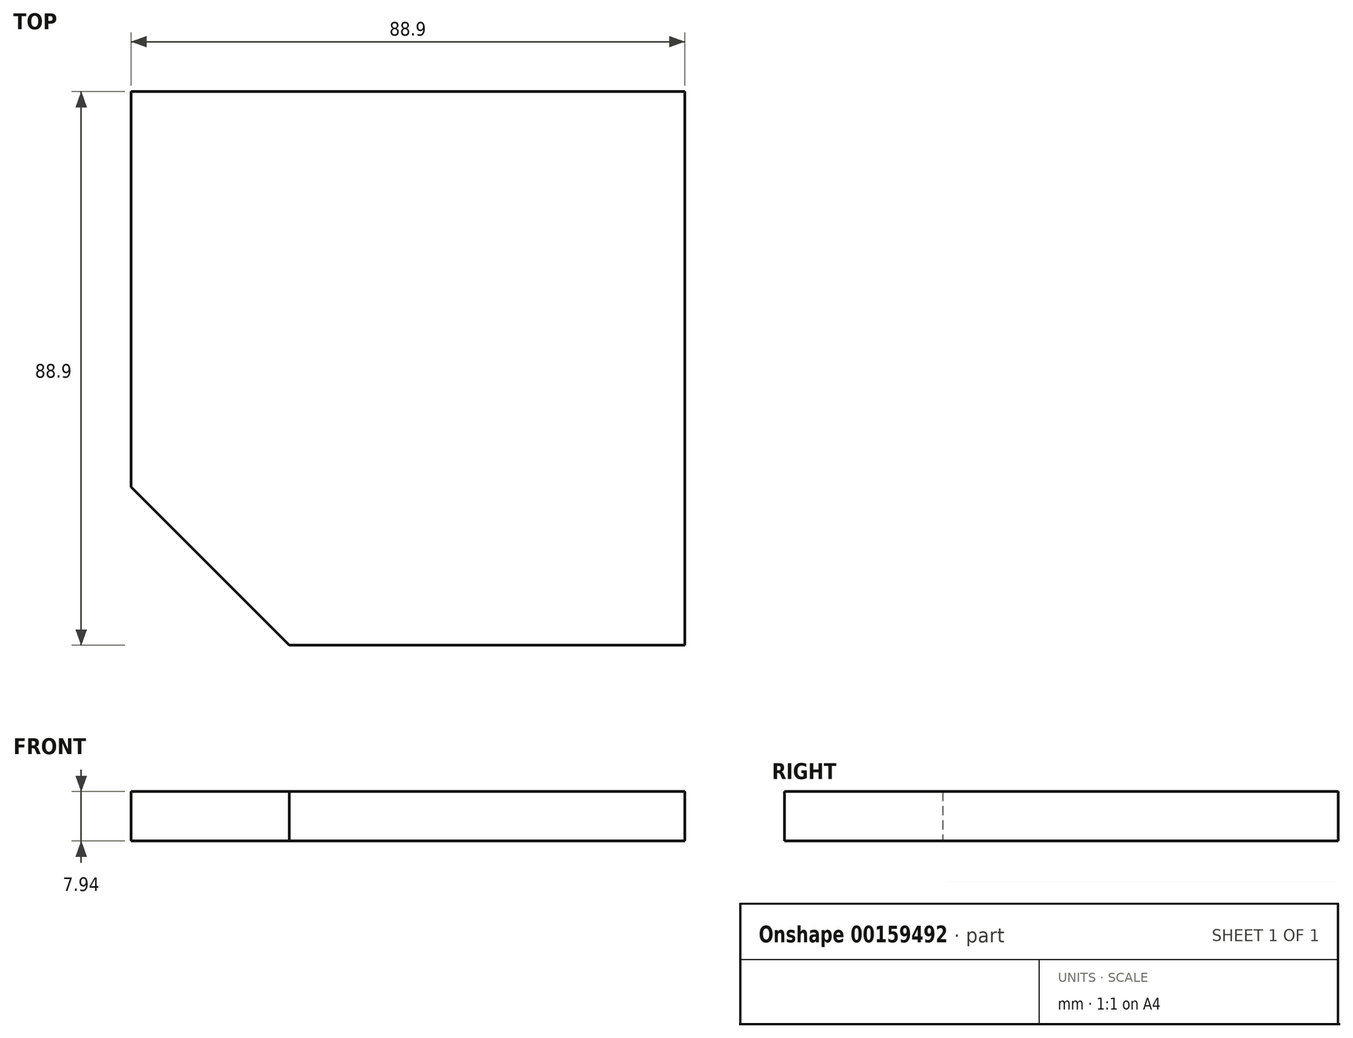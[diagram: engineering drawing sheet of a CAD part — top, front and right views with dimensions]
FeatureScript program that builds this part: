
annotation { "Feature Type Name" : "Feature", "Feature Type Description" : "" }
export const myFeature = defineFeature(function(context is Context, id is Id, definition is map)
    precondition{}
    {
        {
            var Q0;
            Q0=qCreatedBy(makeId("Top.planeOp"),FACE);
            var sketch = newSketch(context, id + "F0", { "sketchPlane" : qUnion([Q0])});
            skLineSegment(sketch, "E0.bottom", {"start": v(-104.26, -7.48) * mm, "end": v(-15.36, -7.48) * mm});
            skLineSegment(sketch, "E0.top", {"start": v(-78.86, -96.38) * mm, "end": v(-15.36, -96.38) * mm});
            skLineSegment(sketch, "E0.left", {"start": v(-104.26, -7.48) * mm, "end": v(-104.26, -70.98) * mm});
            skLineSegment(sketch, "E0.right", {"start": v(-15.36, -7.48) * mm, "end": v(-15.36, -96.38) * mm});
            skLineSegment(sketch, "E1", {"start": v(-104.26, -70.98) * mm, "end": v(-78.86, -96.38) * mm});
            skSolve(sketch);
        }
        {
            var Q0;
            Q0=makeQuery(id+"F0.imprint","IMPRINT",FACE,{"disambiguationData":[TD([[makeQuery(id+"F0.imprint","IMPRINT",EDGE,{"derivedFrom":sQuery(id+"F0.wireOp",EDGE,"E0.bottom")}),-1.0]])]});
            extrude(context, id + "F1", {"entities" : qUnion([Q0]), "depth" : 7.94 * mm});
        }
    });
